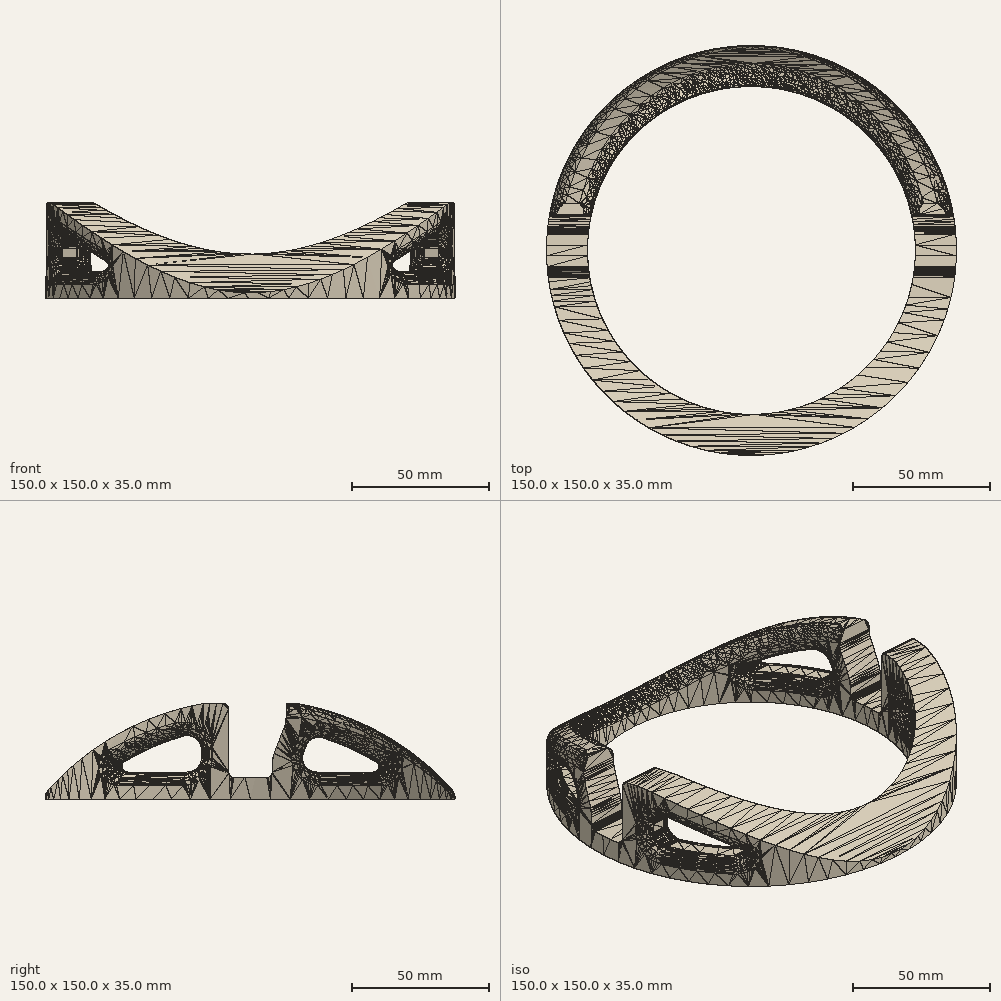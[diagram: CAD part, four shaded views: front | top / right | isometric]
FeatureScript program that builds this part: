
annotation { "Feature Type Name" : "Feature", "Feature Type Description" : "" }
export const myFeature = defineFeature(function(context is Context, id is Id, definition is map)
    precondition{}
    {
        {
            var Q0;
            Q0=qCreatedBy(makeId("Top.planeOp"),FACE);
            var sketch = newSketch(context, id + "F0", { "sketchPlane" : qUnion([Q0])});
            skCircle(sketch, "E0", {"center": v(0, 0) * mm, "radius": 75 * mm});
            skCircle(sketch, "E1", {"center": v(0, 0) * mm, "radius": 60 * mm});
            skSolve(sketch);
        }
        {
            var Q0;
            Q0 = qSketchRegion(id + "F0", true);
            extrude(context, id + "F1", {"entities" : qUnion([Q0]), "depth" : 35 * mm, "offsetDistance" : 25 * mm});
        }
        {
            var Q0;
            Q0=qCreatedBy(makeId("Right.planeOp"),FACE);
            var sketch = newSketch(context, id + "F2", { "sketchPlane" : qUnion([Q0])});
            skLineSegment(sketch, "E2.0", {"start": v(-75, 35) * mm, "end": v(75, 35) * mm});
            skLineSegment(sketch, "E3", {"start": v(-75, 35) * mm, "end": v(-75, 2) * mm});
            skLineSegment(sketch, "E4", {"start": v(75, 35) * mm, "end": v(75, 2) * mm});
            skArc(sketch, "E5", {"start": v(75, 2) * mm, "mid": v(0, 36.51) * mm, "end": v(-75, 2) * mm});
            skSolve(sketch);
        }
        {
            var Q0;
            Q0 = qSketchRegion(id + "F2", true);
            extrude(context, id + "F3", {"entities" : qUnion([Q0]), "operationType" : NewBodyOperationType.REMOVE, "endBound" : BoundingType.SYMMETRIC, "oppositeDirection" : true, "depth" : 200 * mm, "offsetDistance" : 25 * mm});
        }
        {
            var Q0;
            Q0=qCreatedBy(makeId("Right.planeOp"),FACE);
            var sketch = newSketch(context, id + "F4", { "sketchPlane" : qUnion([Q0])});
            skLineSegment(sketch, "E6", {"start": v(-8, 8) * mm, "end": v(-8, 35) * mm});
            skLineSegment(sketch, "E7", {"start": v(13, 35) * mm, "end": v(13, 29.86) * mm});
            skLineSegment(sketch, "E8", {"start": v(12.33, 26.27) * mm, "end": v(8.67, 16.73) * mm});
            skLineSegment(sketch, "E9", {"start": v(8, 13.14) * mm, "end": v(8, 8) * mm});
            skPoint(sketch, "E10.visualSharp", {"position": v(13, 28) * mm});
            skArc(sketch, "E10.filletArc", {"start": v(12.33, 26.27) * mm, "mid": v(12.83, 28.03) * mm, "end": v(13, 29.86) * mm});
            skPoint(sketch, "E11.visualSharp", {"position": v(8, 15) * mm});
            skArc(sketch, "E11.filletArc", {"start": v(8.67, 16.73) * mm, "mid": v(8.17, 14.97) * mm, "end": v(8, 13.14) * mm});
            skLineSegment(sketch, "E12", {"start": v(-8, 35) * mm, "end": v(13, 35) * mm});
            skLineSegment(sketch, "E13", {"start": v(-8, 8) * mm, "end": v(8, 8) * mm});
            skArc(sketch, "E14.0", {"start": v(-24.37, 23.1) * mm, "mid": v(-35.46, 19.12) * mm, "end": v(-45.92, 13.71) * mm});
            skLineSegment(sketch, "E15.0", {"start": v(-44.88, 10) * mm, "end": v(-23, 10) * mm});
            skLineSegment(sketch, "E16.0", {"start": v(-18, 15) * mm, "end": v(-18, 18.3) * mm});
            skPoint(sketch, "E17", {"position": v(0, 8) * mm});
            skArc(sketch, "E18.0", {"start": v(45.92, 13.71) * mm, "mid": v(36.52, 18.65) * mm, "end": v(26.6, 22.43) * mm});
            skLineSegment(sketch, "E19.3", {"start": v(20.43, 19.46) * mm, "end": v(19.4, 16.8) * mm});
            skLineSegment(sketch, "E20.0", {"start": v(24.07, 10) * mm, "end": v(44.88, 10) * mm});
            skPoint(sketch, "E21.visualSharp", {"position": v(-18, 24.67) * mm});
            skArc(sketch, "E21.filletArc", {"start": v(-18, 18.3) * mm, "mid": v(-19.99, 22.28) * mm, "end": v(-24.37, 23.1) * mm});
            skPoint(sketch, "E22.visualSharp", {"position": v(-18, 10) * mm});
            skArc(sketch, "E22.filletArc", {"start": v(-23, 10) * mm, "mid": v(-19.46, 11.46) * mm, "end": v(-18, 15) * mm});
            skPoint(sketch, "E23.visualSharp", {"position": v(-51.56, 10) * mm});
            skArc(sketch, "E23.filletArc", {"start": v(-45.92, 13.71) * mm, "mid": v(-46.8, 11.46) * mm, "end": v(-44.88, 10) * mm});
            skPoint(sketch, "E24.visualSharp", {"position": v(51.56, 10) * mm});
            skArc(sketch, "E24.filletArc", {"start": v(44.88, 10) * mm, "mid": v(46.8, 11.46) * mm, "end": v(45.92, 13.71) * mm});
            skPoint(sketch, "E25.visualSharp", {"position": v(22.07, 23.72) * mm});
            skArc(sketch, "E25.filletArc", {"start": v(26.6, 22.43) * mm, "mid": v(22.92, 22.17) * mm, "end": v(20.43, 19.46) * mm});
            skPoint(sketch, "E26.visualSharp", {"position": v(16.8, 10) * mm});
            skArc(sketch, "E26.filletArc", {"start": v(19.4, 16.8) * mm, "mid": v(19.95, 12.17) * mm, "end": v(24.07, 10) * mm});
            skSolve(sketch);
        }
        {
            var Q0;
            Q0 = qSketchRegion(id + "F4", true);
            extrude(context, id + "F5", {"entities" : qUnion([Q0]), "operationType" : NewBodyOperationType.REMOVE, "endBound" : BoundingType.SYMMETRIC, "depth" : 200 * mm, "offsetDistance" : 25 * mm});
        }
        {
            var Q0;
            {var subQ0=sQuery(id+"F2.wireOp",EDGE,"E5");var subQ1=sQuery(id+"F2.wireOp",EDGE,"E2.0");Q0=makeQuery(id+"F3.boolean.opBoolean","COPY",EDGE,{"disambiguationData":[OD(0.0)],"derivedFrom":makeQuery(id+"F3.opExtrude","SWEPT_EDGE",EDGE,{"disambiguationData":[OSD([subQ1,subQ0]),TDD([makeQuery(id+"F2.imprint","INTERSECT",VERTEX,{"disambiguationData":[OD(0.0)],"derivedFrom":[subQ1,subQ0]})]),OD(0.0)]})});}
            var Q1;
            {var subQ0=sQuery(id+"F2.wireOp",EDGE,"E5");var subQ1=sQuery(id+"F2.wireOp",EDGE,"E2.0");Q1=makeQuery(id+"F3.boolean.opBoolean","COPY",EDGE,{"disambiguationData":[OD(0.0)],"derivedFrom":makeQuery(id+"F3.opExtrude","SWEPT_EDGE",EDGE,{"disambiguationData":[OSD([subQ1,subQ0]),TDD([makeQuery(id+"F2.imprint","INTERSECT",VERTEX,{"disambiguationData":[OD(1.0)],"derivedFrom":[subQ1,subQ0]})]),OD(1.0)]})});}
            var Q2;
            {var subQ0=sQuery(id+"F2.wireOp",EDGE,"E5");var subQ1=sQuery(id+"F2.wireOp",EDGE,"E2.0");Q2=makeQuery(id+"F3.boolean.opBoolean","COPY",EDGE,{"disambiguationData":[OD(1.0)],"derivedFrom":makeQuery(id+"F3.opExtrude","SWEPT_EDGE",EDGE,{"disambiguationData":[OSD([subQ1,subQ0]),TDD([makeQuery(id+"F2.imprint","INTERSECT",VERTEX,{"disambiguationData":[OD(1.0)],"derivedFrom":[subQ1,subQ0]})]),OD(1.0)]})});}
            var Q3;
            {var subQ0=sQuery(id+"F2.wireOp",EDGE,"E5");var subQ1=sQuery(id+"F2.wireOp",EDGE,"E2.0");Q3=makeQuery(id+"F3.boolean.opBoolean","COPY",EDGE,{"disambiguationData":[OD(1.0)],"derivedFrom":makeQuery(id+"F3.opExtrude","SWEPT_EDGE",EDGE,{"disambiguationData":[OSD([subQ1,subQ0]),TDD([makeQuery(id+"F2.imprint","INTERSECT",VERTEX,{"disambiguationData":[OD(0.0)],"derivedFrom":[subQ1,subQ0]})]),OD(0.0)]})});}
            fillet(context, id + "F6", {"entities" : qUnion([Q0, Q1, Q2, Q3]), "radius" : 30 * mm, "tangentPropagation" : true, "allowEdgeOverflow" : false});
        }
        {
            var Q0;
            Q0=makeQuery(id+"F5.boolean.opBoolean","COPY",EDGE,{"disambiguationData":[OD(0.0)],"derivedFrom":makeQuery(id+"F5.opExtrude","SWEPT_EDGE",EDGE,{"disambiguationData":[OSD([sQuery(id+"F4.wireOp",EDGE,"E6"),sQuery(id+"F4.wireOp",EDGE,"E13")])]})});
            var Q1;
            Q1=makeQuery(id+"F5.boolean.opBoolean","COPY",EDGE,{"disambiguationData":[OD(1.0)],"derivedFrom":makeQuery(id+"F5.opExtrude","SWEPT_EDGE",EDGE,{"disambiguationData":[OSD([sQuery(id+"F4.wireOp",EDGE,"E6"),sQuery(id+"F4.wireOp",EDGE,"E13")])]})});
            var Q2;
            Q2=makeQuery(id+"F5.boolean.opBoolean","COPY",EDGE,{"disambiguationData":[OD(0.0)],"derivedFrom":makeQuery(id+"F5.opExtrude","SWEPT_EDGE",EDGE,{"disambiguationData":[OSD([sQuery(id+"F4.wireOp",EDGE,"E9"),sQuery(id+"F4.wireOp",EDGE,"E13")])]})});
            var Q3;
            Q3=makeQuery(id+"F5.boolean.opBoolean","COPY",EDGE,{"disambiguationData":[OD(1.0)],"derivedFrom":makeQuery(id+"F5.opExtrude","SWEPT_EDGE",EDGE,{"disambiguationData":[OSD([sQuery(id+"F4.wireOp",EDGE,"E9"),sQuery(id+"F4.wireOp",EDGE,"E13")])]})});
            var Q4;
            Q4=makeQuery(id+"F5.boolean.opBoolean","COPY",EDGE,{"disambiguationData":[OD(1.0)],"derivedFrom":makeQuery(id+"F5.opExtrude","SWEPT_EDGE",EDGE,{"disambiguationData":[OSD([sQuery(id+"F4.wireOp",EDGE,"E6"),sQuery(id+"F4.wireOp",EDGE,"E12")])]})});
            var Q5;
            Q5=makeQuery(id+"F5.boolean.opBoolean","COPY",EDGE,{"disambiguationData":[OD(1.0)],"derivedFrom":makeQuery(id+"F5.opExtrude","SWEPT_EDGE",EDGE,{"disambiguationData":[OSD([sQuery(id+"F4.wireOp",EDGE,"E7"),sQuery(id+"F4.wireOp",EDGE,"E12")])]})});
            var Q6;
            Q6=makeQuery(id+"F5.boolean.opBoolean","COPY",EDGE,{"disambiguationData":[OD(0.0)],"derivedFrom":makeQuery(id+"F5.opExtrude","SWEPT_EDGE",EDGE,{"disambiguationData":[OSD([sQuery(id+"F4.wireOp",EDGE,"E6"),sQuery(id+"F4.wireOp",EDGE,"E12")])]})});
            var Q7;
            Q7=makeQuery(id+"F5.boolean.opBoolean","COPY",EDGE,{"disambiguationData":[OD(0.0)],"derivedFrom":makeQuery(id+"F5.opExtrude","SWEPT_EDGE",EDGE,{"disambiguationData":[OSD([sQuery(id+"F4.wireOp",EDGE,"E7"),sQuery(id+"F4.wireOp",EDGE,"E12")])]})});
            fillet(context, id + "F7", {"entities" : qUnion([Q0, Q1, Q2, Q3, Q4, Q5, Q6, Q7]), "radius" : 2 * mm, "tangentPropagation" : true, "allowEdgeOverflow" : false});
        }
        {
            var Q0;
            Q0=makeQuery(id+"F5.boolean.opBoolean","INTERSECT",EDGE,{"disambiguationData":[OD(1.0)],"derivedFrom":[makeQuery(id+"F1.opExtrude","SWEPT_FACE",FACE,{"disambiguationData":[OSD([sQuery(id+"F0.wireOp",EDGE,"E0")])]}),makeQuery(id+"F5.opExtrude","SWEPT_FACE",FACE,{"disambiguationData":[OSD([sQuery(id+"F4.wireOp",EDGE,"E15.0")])]})]});
            var Q1;
            Q1=makeQuery(id+"F5.boolean.opBoolean","INTERSECT",EDGE,{"disambiguationData":[OD(1.0)],"derivedFrom":[makeQuery(id+"F1.opExtrude","SWEPT_FACE",FACE,{"disambiguationData":[OSD([sQuery(id+"F0.wireOp",EDGE,"E0")])]}),makeQuery(id+"F5.opExtrude","SWEPT_FACE",FACE,{"disambiguationData":[OSD([sQuery(id+"F4.wireOp",EDGE,"E20.0")])]})]});
            var Q2;
            Q2=makeQuery(id+"F5.boolean.opBoolean","INTERSECT",EDGE,{"disambiguationData":[OD(0.0)],"derivedFrom":[makeQuery(id+"F1.opExtrude","SWEPT_FACE",FACE,{"disambiguationData":[OSD([sQuery(id+"F0.wireOp",EDGE,"E1")])]}),makeQuery(id+"F5.opExtrude","SWEPT_FACE",FACE,{"disambiguationData":[OSD([sQuery(id+"F4.wireOp",EDGE,"E15.0")])]})]});
            var Q3;
            Q3=makeQuery(id+"F5.boolean.opBoolean","INTERSECT",EDGE,{"disambiguationData":[OD(0.0)],"derivedFrom":[makeQuery(id+"F1.opExtrude","SWEPT_FACE",FACE,{"disambiguationData":[OSD([sQuery(id+"F0.wireOp",EDGE,"E1")])]}),makeQuery(id+"F5.opExtrude","SWEPT_FACE",FACE,{"disambiguationData":[OSD([sQuery(id+"F4.wireOp",EDGE,"E20.0")])]})]});
            var Q4;
            Q4=makeQuery(id+"F5.boolean.opBoolean","INTERSECT",EDGE,{"disambiguationData":[OD(1.0)],"derivedFrom":[makeQuery(id+"F1.opExtrude","SWEPT_FACE",FACE,{"disambiguationData":[OSD([sQuery(id+"F0.wireOp",EDGE,"E1")])]}),makeQuery(id+"F5.opExtrude","SWEPT_FACE",FACE,{"disambiguationData":[OSD([sQuery(id+"F4.wireOp",EDGE,"E15.0")])]})]});
            var Q5;
            Q5=makeQuery(id+"F5.boolean.opBoolean","INTERSECT",EDGE,{"disambiguationData":[OD(1.0)],"derivedFrom":[makeQuery(id+"F1.opExtrude","SWEPT_FACE",FACE,{"disambiguationData":[OSD([sQuery(id+"F0.wireOp",EDGE,"E1")])]}),makeQuery(id+"F5.opExtrude","SWEPT_FACE",FACE,{"disambiguationData":[OSD([sQuery(id+"F4.wireOp",EDGE,"E20.0")])]})]});
            var Q6;
            Q6=makeQuery(id+"F5.boolean.opBoolean","INTERSECT",EDGE,{"disambiguationData":[OD(0.0)],"derivedFrom":[makeQuery(id+"F1.opExtrude","SWEPT_FACE",FACE,{"disambiguationData":[OSD([sQuery(id+"F0.wireOp",EDGE,"E0")])]}),makeQuery(id+"F5.opExtrude","SWEPT_FACE",FACE,{"disambiguationData":[OSD([sQuery(id+"F4.wireOp",EDGE,"E20.0")])]})]});
            var Q7;
            Q7=makeQuery(id+"F5.boolean.opBoolean","INTERSECT",EDGE,{"disambiguationData":[OD(0.0)],"derivedFrom":[makeQuery(id+"F1.opExtrude","SWEPT_FACE",FACE,{"disambiguationData":[OSD([sQuery(id+"F0.wireOp",EDGE,"E0")])]}),makeQuery(id+"F5.opExtrude","SWEPT_FACE",FACE,{"disambiguationData":[OSD([sQuery(id+"F4.wireOp",EDGE,"E15.0")])]})]});
            fillet(context, id + "F8", {"entities" : qUnion([Q0, Q1, Q2, Q3, Q4, Q5, Q6, Q7]), "radius" : 5 * mm, "tangentPropagation" : true, "allowEdgeOverflow" : false});
        }
        {
            var Q0;
            {var subQ0=sQuery(id+"F2.wireOp",EDGE,"E5");Q0=makeQuery(id+"F3.boolean.opBoolean","INTERSECT",EDGE,{"derivedFrom":[makeQuery(id+"F1.opExtrude","SWEPT_FACE",FACE,{"disambiguationData":[OSD([sQuery(id+"F0.wireOp",EDGE,"E0")])]}),makeQuery(id+"F3.opExtrude","SWEPT_FACE",FACE,{"disambiguationData":[OSD([subQ0]),TDD([makeQuery(id+"F2.imprint","IMPRINT",EDGE,{"disambiguationData":[TD([[makeQuery(id+"F2.imprint","INTERSECT",VERTEX,{"derivedFrom":[sQuery(id+"F2.wireOp",EDGE,"E4"),subQ0]}),-1.0]])],"derivedFrom":subQ0})])]})]});}
            var Q1;
            {var subQ0=sQuery(id+"F2.wireOp",EDGE,"E5");Q1=makeQuery(id+"F3.boolean.opBoolean","INTERSECT",EDGE,{"derivedFrom":[makeQuery(id+"F1.opExtrude","SWEPT_FACE",FACE,{"disambiguationData":[OSD([sQuery(id+"F0.wireOp",EDGE,"E1")])]}),makeQuery(id+"F3.opExtrude","SWEPT_FACE",FACE,{"disambiguationData":[OSD([subQ0]),TDD([makeQuery(id+"F2.imprint","IMPRINT",EDGE,{"disambiguationData":[TD([[makeQuery(id+"F2.imprint","INTERSECT",VERTEX,{"derivedFrom":[sQuery(id+"F2.wireOp",EDGE,"E4"),subQ0]}),-1.0]])],"derivedFrom":subQ0})])]})]});}
            fillet(context, id + "F9", {"entities" : qUnion([Q0, Q1]), "radius" : 5 * mm, "tangentPropagation" : true, "allowEdgeOverflow" : false});
        }
    });
